# Revit family: 1STERN_FAUCET_TOUCHLESS_CSABA
name_source: partatom
category: Generic Models
revit_build: Autodesk Revit 2017 (Build: 20160225_1515(x64)
units: mm (PartAtom-declared; Revit-internal decimal feet)

## family parameters
Can host rebar = No
Cut with Voids When Loaded = No
Host = Face
Part Type = Normal
Room Calculation Point = No
Round Connector Dimension = Use Diameter
Shared = No

## types (2) — shared parameters
AVAILABLE FINISHES = Brushed Nickel - Matt Black - Satin Gold - PVD Antique Bronze - PVD rose Gold - PVD Copper - AISI316 Material
BADGE = https://bim.archiproducts.com
Default Elevation = 1219 mm
Description = CSABA is a touch-free deck-mounted electronic faucet.‎ For cold or premixed water.‎ Chrome plated body, other finishes available.‎ Activated by concealed sensor built into the spout.‎ Filter included.‎ Sensor includes a low battery ndicator.‎ Adjustable settings by remote control: sensor range, security time, delay in, delay out, on-off and reset to factory settings.‎
FINISHING MATERIAL = Chrome - Stern
INSTALLATION = Deck mounted
MATERIAL DESCRIPTION = Finish: Chrome
Manufacturer = Stern Engineering
OPERATING PRESSURE = 0.5 - 8.0 BAR (7- 116  PSI). With a pressure over 8 bar, use a pressure reducing valve.
OPTIONS = Remote control (code 07100005)
PRODUCT SHEET = https://www.archiproducts.com
SECURITY TIME = Auto shutoff after 90 seconds. Adjustableby remote control.
TECHNICAL SHEET = http://www.sternfaucets.com
URL = http://www.sternfaucets.com
VOLTAGE = 9 V
WATER FLOW = 0 GPM
WATER SAVING OPTIONS = 0.5 GPM/1.89 LPM, 1.0 GPM/4 LPM - PCA spray
WATER SUPPLY = Cold or premixed water
WATER TEMPERATURE = 70°C Maximum
WIDTH = 50 mm  [stored 0.164042 ft]

## per-type parameters (varying)
| type | DEPTH | HEIGHT | Model | POWER SUPPLY | PRODUCT CODE |
| CSABA - 9V BATTERY | 130 mm  [stored 0.426509 ft] | 225 mm  [stored 0.738189 ft] | Csaba B | IP67 Dual power input box with a 9V battery (battery not included) | 233000 |
| CSABA - 9V TRANSFORMER | 144 mm  [stored 0.472441 ft] | 255 mm  [stored 0.836614 ft] | Csaba E | IP67 Dual power input box with a 9V trasformer | 233010 |

note: [stored X ft] marks values corroborated as IEEE doubles in the binary element streams (Revit-internal decimal feet)

## geometry (parser evidence)
native form markers: Sweep x2
no freeform markers — native parametric forms only
